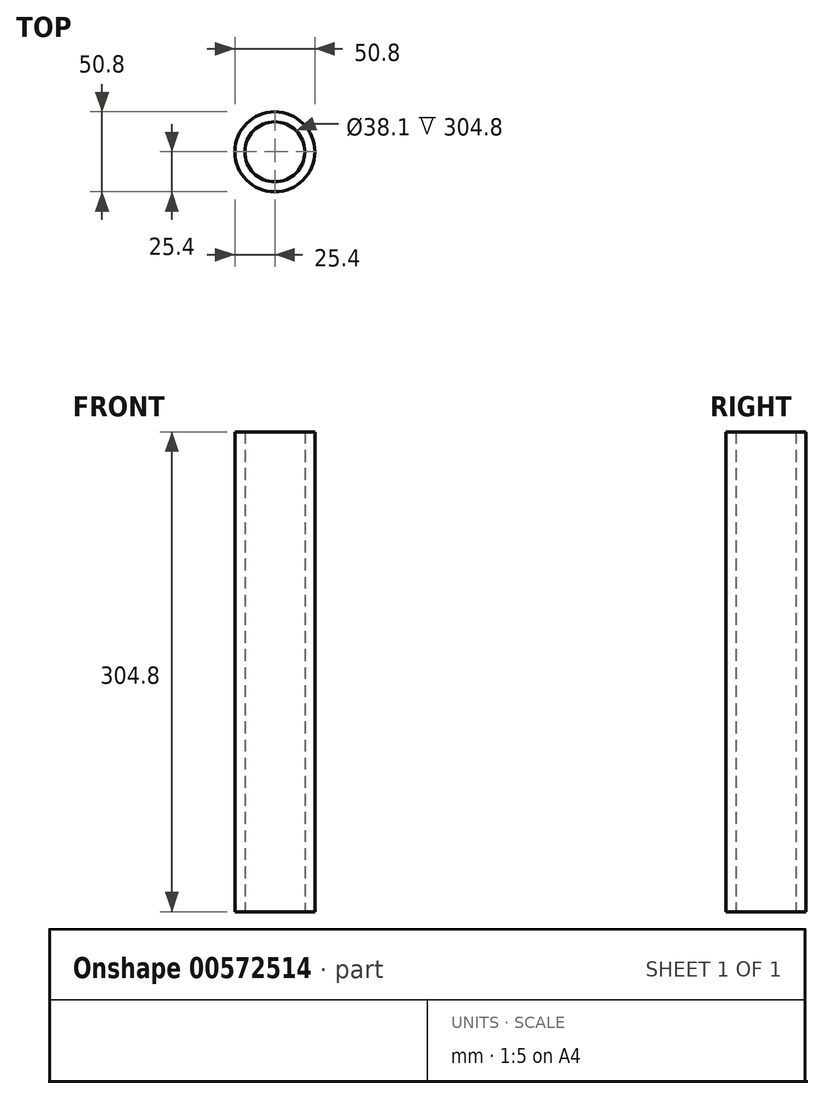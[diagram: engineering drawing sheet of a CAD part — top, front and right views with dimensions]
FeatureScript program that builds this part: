
annotation { "Feature Type Name" : "Feature", "Feature Type Description" : "" }
export const myFeature = defineFeature(function(context is Context, id is Id, definition is map)
    precondition{}
    {
        {
            var Q0;
            Q0=qCreatedBy(makeId("Top.planeOp"),FACE);
            var sketch = newSketch(context, id + "F0", { "sketchPlane" : qUnion([Q0])});
            skCircle(sketch, "E0", {"center": v(0, 0) * mm, "radius": 25.4 * mm});
            skCircle(sketch, "E1", {"center": v(0, 0) * mm, "radius": 19.05 * mm});
            skSolve(sketch);
        }
        {
            var Q0;
            Q0 = qSketchRegion(id + "F0", true);
            extrude(context, id + "F1", {"entities" : qUnion([Q0]), "depth" : 304.8 * mm, "offsetDistance" : 25.4 * mm});
        }
    });
